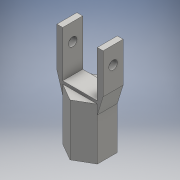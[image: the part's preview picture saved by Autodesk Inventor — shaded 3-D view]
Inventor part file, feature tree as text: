
AUTODESK INVENTOR PART (.ipt)
format: ipt  version: 2016 (Build 200138000, 138)  size: 147,456 bytes
history: native  units: mm
features: extrude x6, sketch x6
ambient origin geometry x8: Origin, YZ Plane, XZ Plane, XY Plane, X Axis, Y Axis, Z Axis, Center Point
bodies: Solid1 (feature_tree)
feature tree (12):
  extrude  "Extrusion1"  Depth=18.0mm TaperAngle=0.0deg
  extrude  "Extrusion2"  Depth=14.0mm TaperAngle=0.0deg
  extrude  "Extrusion3"  Depth=2.0mm
  extrude  "Extrusion4"  Depth=6.928203mm
  extrude  "Extrusion5"  Depth=6.928203mm TaperAngle=0.0deg
  extrude  "Extrusion6"  Depth=6.928203mm TaperAngle=0.0deg
  sketch  "Sketch1"  dims[d1=12.0mm d3=18.0mm d4=0.0mm]
  sketch  "Sketch2"  dims[d5=6.2mm d6=14.0mm d7=0.0mm]
  sketch  "Sketch3"  dims[d8=17.0mm d9=0.0mm d10=2.0mm]
  sketch  "Sketch4"  dims[d11=2.0mm d12=6.928203mm]
  sketch  "Sketch5"  dims[d13=6.928203mm d14=0.0mm d15=6.928203mm d16=0.0mm]
  sketch  "Sketch6"  dims[d18=3.0mm d19=6.928203mm d20=0.0mm]
